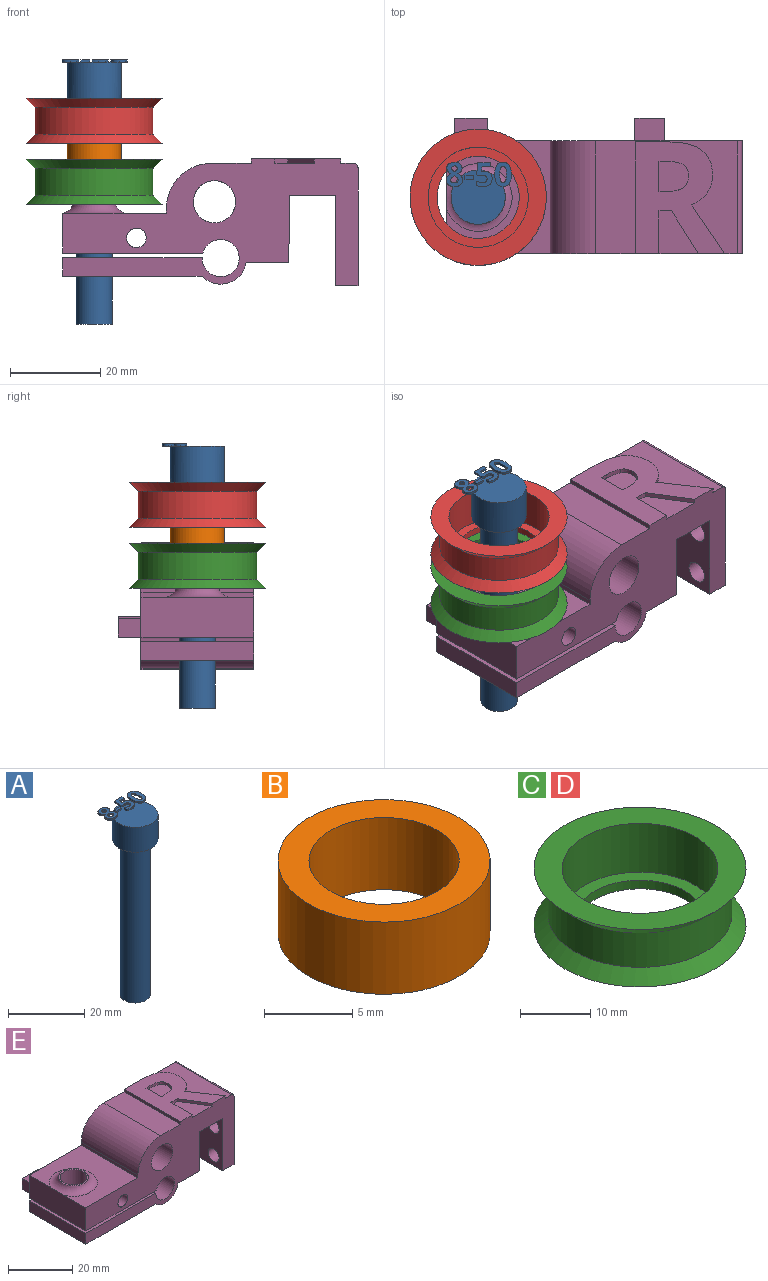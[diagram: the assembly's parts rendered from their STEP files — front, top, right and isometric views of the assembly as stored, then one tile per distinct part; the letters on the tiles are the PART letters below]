
ASSEMBLY  parts=5 mates=4
PART A: 86 faces, bbox 14.5x13.7x58.5 mm
  f0: plane 12x12mm, normal (0,0,1), area 99.4mm2, adj f5,f22,f23,f24,f25,f26,f40,f41
  f1: plane 1x0.26mm, normal (0,0,1), area 0.1mm2, adj f5,f46,f47,f48,f49
  f2: plane 0.85x0.68mm, normal (0,0,1), area 0.2mm2, adj f5,f29,f30,f31
  f3: cylinder r=4mm len=50mm, axis (0,0,-1), area 1256.6mm2, adj f4,f6
  f4: plane 8x8mm, normal (0,0,-1), area 50.3mm2, adj f3
  f5: cylinder r=6mm len=12mm, axis (0,0,-1), area 301.6mm2, adj f0,f1,f2,f6,f39,f45,f67,f85
  f6: plane 12x12mm, normal (0,0,-1), area 62.8mm2, adj f3,f5
  f7: extruded ~0.5x0.46mm, area 0.2mm2, adj f8,f37,f38,f39
  f8: extruded ~0.5x0.46mm, area 0.2mm2, adj f7,f9,f38,f39
  f9: extruded ~0.5x0.39mm, area 0.2mm2, adj f8,f10,f38,f39
  f10: extruded ~0.5x0.4mm, area 0.2mm2, adj f9,f11,f38,f39
  f11: extruded ~0.5x0.49mm, area 0.3mm2, adj f10,f12,f38,f39
  f12: extruded ~0.5x0.5mm, area 0.3mm2, adj f11,f13,f38,f39
  f13: extruded ~0.5x0.39mm, area 0.2mm2, adj f12,f37,f38,f39
  f14: extruded ~1.22x0.5mm, area 0.6mm2, adj f15,f35,f38,f39
  f15: extruded ~1.22x0.5mm, area 0.6mm2, adj f14,f16,f38,f39
  f16: extruded ~0.91x0.5mm, area 0.5mm2, adj f15,f17,f38,f39
  f17: extruded ~0.71x0.5mm, area 0.4mm2, adj f16,f18,f38,f39
  f18: extruded ~0.65x0.61mm, area 0.4mm2, adj f17,f19,f38,f39
  f19: extruded ~0.77x0.62mm, area 0.5mm2, adj f18,f20,f38,f39
  f20: extruded ~0.8x0.5mm, area 0.4mm2, adj f19,f21,f38,f39
  f21: extruded ~1.04x0.5mm, area 0.6mm2, adj f20,f22,f38,f39
  f22: extruded ~1.36x0.5mm, area 0.7mm2, adj f0,f21,f23,f38,f39
  f23: extruded ~1.33x0.5mm, area 0.7mm2, adj f0,f22,f24,f38
  f24: extruded ~1.04x0.51mm, area 0.6mm2, adj f0,f23,f25,f38
  f25: extruded ~0.75x0.5mm, area 0.4mm2, adj f0,f24,f26,f38
  f26: extruded ~0.85x0.66mm, area 0.5mm2, adj f0,f25,f27,f38,f39
  f27: extruded ~0.72x0.56mm, area 0.5mm2, adj f26,f28,f38,f39
  f28: extruded ~0.72x0.5mm, area 0.4mm2, adj f27,f35,f38,f39
  f29: extruded ~0.5x0.45mm, area 0.3mm2, adj f2,f30,f36,f38,f39
  f30: extruded ~0.5x0.47mm, area 0.3mm2, adj f2,f29,f31,f38
  f31: extruded ~0.62x0.5mm, area 0.3mm2, adj f2,f30,f32,f38,f39
  f32: extruded ~0.59x0.5mm, area 0.3mm2, adj f31,f33,f38,f39
  f33: extruded ~0.5x0.48mm, area 0.3mm2, adj f32,f34,f38,f39
  f34: extruded ~0.89x0.77mm, area 0.6mm2, adj f33,f36,f38,f39
  f35: extruded ~0.93x0.5mm, area 0.5mm2, adj f14,f28,f38,f39
  f36: extruded ~0.66x0.5mm, area 0.4mm2, adj f29,f34,f38,f39
  f37: extruded ~0.5x0.39mm, area 0.2mm2, adj f7,f13,f38,f39
  f38: plane 5.4x3.69mm, normal (0,0,1), area 12.7mm2, adj f7,f8,f9,f10,f11,f12,f13,f14
  f39: plane 5.4x3.53mm, normal (0,0,-1), area 10.2mm2, adj f5,f7,f8,f9,f10,f11,f12,f13
  f40: plane 0.9x0.5mm, normal (-1,0,0), area 0.4mm2, adj f0,f41,f43,f44
  f41: plane 1.93x0.5mm, normal (0,-1,0), area 1mm2, adj f0,f40,f42,f44
  f42: plane 0.9x0.5mm, normal (1,0,0), area 0.4mm2, adj f0,f41,f43,f44
  f43: plane 1.93x0.5mm, normal (0,1,0), area 1mm2, adj f0,f40,f42,f44
  f44: plane 1.93x0.9mm, normal (0,0,1), area 1.7mm2, adj f40,f41,f42,f43
  f45: plane 0.76x0.31mm, normal (0,0,-1), area 0mm2, adj f5,f46
  f46: extruded ~1.21x0.5mm, area 0.7mm2, adj f0,f1,f45,f47,f65,f66
  f47: extruded ~0.54x0.5mm, area 0.3mm2, adj f1,f46,f48,f66
  f48: plane 0.5x0.13mm, normal (-0.2,0.98,0), area 0.1mm2, adj f1,f47,f49,f66
  f49: plane 1.03x0.5mm, normal (1,-0.09,0), area 0.5mm2, adj f1,f48,f50,f66,f67
  f50: plane 1.88x0.5mm, normal (0,-1,0), area 0.9mm2, adj f49,f51,f66,f67
  f51: plane 0.94x0.5mm, normal (1,0,0), area 0.5mm2, adj f50,f52,f66,f67
  f52: plane 2.85x0.5mm, normal (0,1,0), area 1.4mm2, adj f51,f53,f66,f67
  f53: plane 2.68x0.5mm, normal (-1,0.07,0), area 1.3mm2, adj f0,f52,f54,f66,f67
  f54: plane 0.5x0.44mm, normal (-0.47,-0.88,0), area 0.3mm2, adj f0,f53,f55,f66
  f55: extruded ~0.5x0.37mm, area 0.2mm2, adj f0,f54,f56,f66
  f56: extruded ~0.5x0.42mm, area 0.2mm2, adj f0,f55,f57,f66
  f57: extruded ~1.05x0.8mm, area 0.8mm2, adj f0,f56,f58,f66
  f58: extruded ~1.02x0.83mm, area 0.8mm2, adj f0,f57,f59,f66
  f59: extruded ~0.72x0.5mm, area 0.4mm2, adj f0,f58,f60,f66
  f60: extruded ~0.66x0.5mm, area 0.4mm2, adj f0,f59,f61,f66
  f61: plane 0.96x0.5mm, normal (-1,0,0), area 0.5mm2, adj f0,f60,f62,f66
  f62: extruded ~1.42x0.5mm, area 0.7mm2, adj f0,f61,f63,f66
  f63: extruded ~1.55x0.5mm, area 0.8mm2, adj f0,f62,f64,f66
  f64: extruded ~1.36x0.54mm, area 0.8mm2, adj f0,f63,f65,f66
  f65: extruded ~1.17x0.5mm, area 0.6mm2, adj f0,f46,f64,f66
  f66: plane 5.33x3.51mm, normal (0,0,1), area 10.9mm2, adj f46,f47,f48,f49,f50,f51,f52,f53
  f67: plane 2.97x1.71mm, normal (0,0,-1), area 3.5mm2, adj f5,f49,f50,f51,f52,f53
  f68: extruded ~1.39x0.5mm, area 0.7mm2, adj f69,f83,f84,f85
  f69: extruded ~1.39x0.5mm, area 0.7mm2, adj f68,f70,f84,f85
  f70: extruded ~0.56x0.5mm, area 0.4mm2, adj f69,f71,f84,f85
  f71: extruded ~0.56x0.5mm, area 0.4mm2, adj f70,f72,f84,f85
  f72: extruded ~1.39x0.5mm, area 0.7mm2, adj f71,f73,f84,f85
  f73: extruded ~1.38x0.5mm, area 0.7mm2, adj f72,f74,f84,f85
  f74: extruded ~0.56x0.5mm, area 0.4mm2, adj f73,f83,f84,f85
  f75: extruded ~2.04x0.5mm, area 1.1mm2, adj f76,f82,f84,f85
  f76: extruded ~2.02x0.5mm, area 1.1mm2, adj f75,f77,f84,f85
  f77: extruded ~1.38x0.69mm, area 0.8mm2, adj f76,f78,f84,f85
  f78: extruded ~1.38x0.66mm, area 0.8mm2, adj f77,f79,f84,f85
  f79: extruded ~2.05x0.5mm, area 1.1mm2, adj f78,f80,f84,f85
  f80: extruded ~2.02x0.5mm, area 1mm2, adj f0,f79,f81,f84,f85
  f81: extruded ~1.37x0.68mm, area 0.8mm2, adj f0,f80,f82,f84
  f82: extruded ~1.39x0.66mm, area 0.8mm2, adj f0,f75,f81,f84,f85
  f83: extruded ~0.56x0.5mm, area 0.4mm2, adj f68,f74,f84,f85
  f84: plane 5.41x3.68mm, normal (0,0,1), area 12.1mm2, adj f68,f69,f70,f71,f72,f73,f74,f75
  f85: plane 5.41x3.68mm, normal (0,0,-1), area 10.3mm2, adj f5,f68,f69,f70,f71,f72,f73,f74
PART B: 4 faces, bbox 12x12x5 mm
  f0: cylinder r=4.25mm len=8.5mm, axis (0,0,-1), area 133.5mm2, adj f2,f3
  f1: cylinder r=6mm len=12mm, axis (0,0,-1), area 188.5mm2, adj f2,f3
  f2: plane 12x12mm, normal (0,0,1), area 56.4mm2, adj f0,f1
  f3: plane 12x12mm, normal (0,0,-1), area 56.4mm2, adj f0,f1
PART C: 8 faces, bbox 30.2x30.2x10 mm
  f0: plane 30.2x30.2mm, normal (0,0,1), area 329.2mm2, adj f1,f7
  f1: cylinder r=11.1mm len=22.2mm, axis (0,0,-1), area 592.8mm2, adj f0,f2
  f2: plane 22.2x22.2mm, normal (0,0,1), area 126.9mm2, adj f1,f3
  f3: cylinder r=9.1mm len=18.2mm, axis (0,0,-1), area 85.8mm2, adj f2,f4
  f4: plane 30.2x30.2mm, normal (0,0,-1), area 456.2mm2, adj f3,f5
  f5: cone r=13.1mm half-angle=45deg, axis (0,0,-1), area 250.6mm2, adj f4,f6
  f6: cylinder r=13.1mm len=26.2mm, axis (0,0,-1), area 493.9mm2, adj f5,f7
  f7: cone r=15.1mm half-angle=45deg, axis (0,0,1), area 250.6mm2, adj f0,f6
PART D: same geometry as C
PART E: 63 faces, bbox 68.9x30x28.1 mm
  f0: plane 31.42x25mm, normal (0,0,1), area 392.1mm2, adj f14,f15,f32,f34,f47,f48,f49,f50
  f1: plane 9.51x8.71mm, normal (0,0,1), area 54.7mm2, adj f14,f44,f45,f46
  f2: plane 25x8.82mm, normal (-1,0,0), area 219.6mm2, adj f7,f14,f15,f20,f31
  f3: cylinder r=4.17mm len=10.78mm, axis (0,0,1), area 282.8mm2, adj f20,f22
  f4: plane 25x9.44mm, normal (0,0,-1), area 236mm2, adj f13,f14,f15,f17
  f5: plane 30.88x25mm, normal (0,0,-1), area 717.2mm2, adj f6,f14,f15,f16,f17
  f6: plane 25x4.12mm, normal (-1,0,0), area 103mm2, adj f5,f14,f15,f21
  f7: plane 25x23mm, normal (0,0,1), area 400mm2, adj f2,f8,f14,f15,f31
  f8: plane 25x1.1mm, normal (-1,0,0), area 27.5mm2, adj f7,f14,f15,f32
  f9: plane 26.09x25mm, normal (1,0,0), area 581.6mm2, adj f10,f14,f15,f23,f24,f29,f30,f34
  f10: plane 25x5mm, normal (0,0,-1), area 125mm2, adj f9,f11,f14,f15
  f11: plane 25x20mm, normal (-1,0,0), area 429.3mm2, adj f10,f12,f14,f15,f23,f24,f29,f30
  f12: plane 25x10.2mm, normal (0,0,-1), area 255mm2, adj f11,f13,f14,f15
  f13: plane 25x14.91mm, normal (1,0,-0.01), area 335.8mm2, adj f4,f12,f14,f15,f26,f28
  f14: plane 65.42x28.09mm, normal (0,-1,0), area 1008.7mm2, adj f0,f1,f2,f4,f5,f6,f7,f8
  f15: plane 65.42x27.09mm, normal (0,1,0), area 937.7mm2, adj f0,f2,f4,f5,f6,f7,f8,f9
  f16: cylinder r=4.17mm len=8.35mm, axis (0,0,1), area 108.1mm2, adj f5,f21
  f17: cylinder r=5.75mm len=25mm, axis (0,-1,0), area 315.9mm2, adj f4,f5,f14,f15
  f18: cylinder r=2.17mm len=25mm, axis (0,-1,0), area 341.6mm2, adj f14,f15
  f19: cylinder r=4.1mm len=25mm, axis (0,-1,0), area 618.7mm2, adj f14,f15,f20,f21
  f20: plane 31.07x30mm, normal (0,0,-1), area 758.4mm2, adj f2,f3,f14,f15,f19,f36,f37,f38
  f21: plane 30.91x25mm, normal (0,0,1), area 718.1mm2, adj f6,f14,f15,f16,f19
  f22: plane 9.35x9.35mm, normal (0,0,1), area 13.9mm2, adj f3,f31
  f23: cylinder r=2.43mm len=5mm, axis (1,0,0), area 76.2mm2, adj f9,f11
  f24: cylinder r=2.2mm len=5mm, axis (1,0,0), area 69.1mm2, adj f9,f11
  f25: plane 4.85x4.85mm, normal (1,0,0), area 18.5mm2, adj f26
  f26: cylinder r=2.43mm len=9.78mm, axis (1,0,0), area 148.8mm2, adj f13,f25
  f27: plane 4.85x4.85mm, normal (1,0,0), area 18.5mm2, adj f28
  f28: cylinder r=2.43mm len=9.78mm, axis (1,0,0), area 148.8mm2, adj f13,f27
  f29: cylinder r=2.43mm len=5mm, axis (1,0,0), area 76.2mm2, adj f9,f11
  f30: cylinder r=2.43mm len=5mm, axis (1,0,0), area 76.2mm2, adj f9,f11
  f31: torus R=7.5mm, axis (0,0,-1), area 134.6mm2, adj f2,f7,f22
  f32: cylinder r=10mm len=25mm, axis (0,-1,0), area 392.7mm2, adj f0,f8,f14,f15
  f33: cylinder r=4.68mm len=25mm, axis (0,-1,0), area 735.2mm2, adj f14,f15
  f34: cylinder r=1mm len=25mm, axis (0,-1,0), area 39.3mm2, adj f0,f9,f14,f15
  f35: plane 7.3x5mm, normal (0,0,1), area 36.5mm2, adj f15,f36,f37,f38
  f36: plane 5x4.12mm, normal (-1,0,0), area 20.6mm2, adj f15,f20,f35,f38
  f37: plane 5x4.12mm, normal (1,0,0), area 20.6mm2, adj f15,f20,f35,f38
  f38: plane 7.3x4.12mm, normal (0,1,0), area 30.1mm2, adj f20,f35,f36,f37
  f39: plane 6.63x5mm, normal (0,0,1), area 33.2mm2, adj f15,f40,f42,f43
  f40: plane 5x4.5mm, normal (-1,0,0), area 22.5mm2, adj f15,f39,f41,f43
  f41: plane 6.63x5mm, normal (0,0,-1), area 33.2mm2, adj f15,f40,f42,f43
  f42: plane 5x4.5mm, normal (1,0,0), area 22.5mm2, adj f15,f39,f41,f43
  f43: plane 6.63x4.5mm, normal (0,1,0), area 29.9mm2, adj f39,f40,f41,f42
  f44: plane 9.51x1mm, normal (1,0,0), area 9.5mm2, adj f1,f14,f45,f61
  f45: plane 2.79x1mm, normal (0,-1,0), area 2.8mm2, adj f1,f44,f46,f61
  f46: plane 9.51x5.92mm, normal (-0.85,-0.53,0), area 11.2mm2, adj f1,f14,f45,f61
  f47: extruded ~10.8x7.29mm, area 13mm2, adj f0,f14,f48,f61
  f48: extruded ~3.41x2.67mm, area 4.4mm2, adj f0,f47,f49,f61
  f49: extruded ~3.89x1.2mm, area 4.1mm2, adj f0,f48,f50,f61
  f50: extruded ~5.59x2.42mm, area 6.3mm2, adj f0,f49,f51,f61
  f51: extruded ~7.48x1.84mm, area 7.8mm2, adj f0,f50,f52,f61
  f52: plane 7.22x1mm, normal (0,1,0), area 7.2mm2, adj f0,f51,f53,f61
  f53: plane 24.79x1mm, normal (-1,0,0), area 24.8mm2, adj f0,f14,f52,f61
  f54: plane 1.69x1mm, normal (0,1,0), area 1.7mm2, adj f55,f60,f61,f62
  f55: plane 6.7x1mm, normal (1,0,0), area 6.7mm2, adj f54,f56,f61,f62
  f56: plane 1.6x1mm, normal (0,-1,0), area 1.6mm2, adj f55,f57,f61,f62
  f57: extruded ~3.75x1mm, area 3.9mm2, adj f56,f58,f61,f62
  f58: extruded ~2.51x1.21mm, area 2.9mm2, adj f57,f59,f61,f62
  f59: extruded ~2.61x1.19mm, area 3mm2, adj f58,f60,f61,f62
  f60: extruded ~3.68x1mm, area 3.8mm2, adj f54,f59,f61,f62
  f61: plane 24.79x19.8mm, normal (0,0,1), area 300mm2, adj f14,f44,f45,f46,f47,f48,f49,f50
  f62: plane 6.7x6.56mm, normal (0,0,1), area 38.8mm2, adj f54,f55,f56,f57,f58,f59,f60
PLACE A t=(-103.78,-12.5,-13.6)mm
PLACE B rot(axis=(1,0,0),180deg) t=(-103.78,-12.5,26.4)mm
PLACE C t=(-103.78,-12.5,18.1)mm
PLACE D t=(-103.78,-12.5,31.6)mm
PLACE E at identity
MATE fastened A.f3 <-> D.f1  axis (0,0,-1) through (-103.78,-12.5,36.4)mm
MATE fastened B.f0 <-> C.f1  axis (0,0,1) through (-103.78,-12.5,21.4)mm
MATE fastened C.f1 <-> E.f3  axis (0,0,-1) through (-103.78,-12.5,12.9)mm
MATE fastened D.f1 <-> B.f0  axis (0,0,-1) through (-103.78,-12.5,26.4)mm
